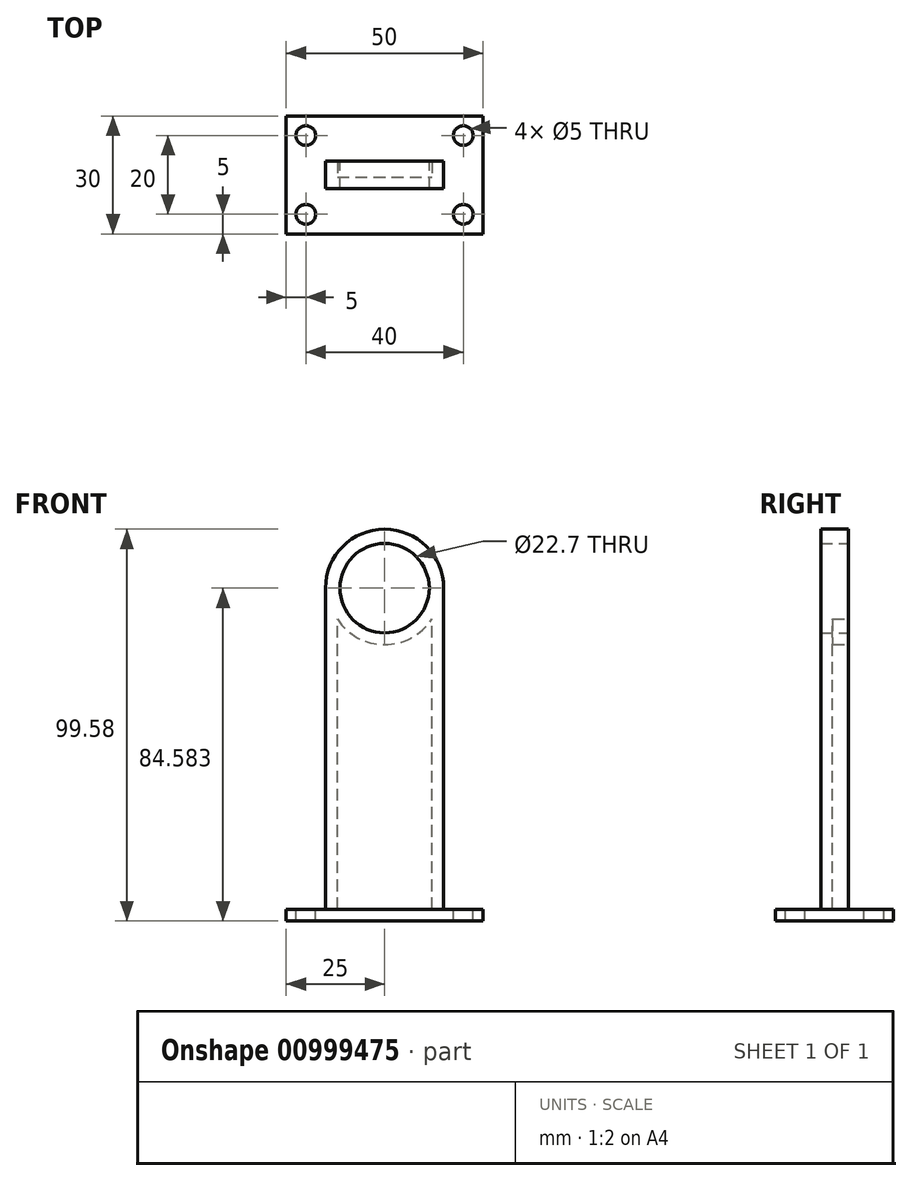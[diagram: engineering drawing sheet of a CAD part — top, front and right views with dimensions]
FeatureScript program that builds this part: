
annotation { "Feature Type Name" : "Feature", "Feature Type Description" : "" }
export const myFeature = defineFeature(function(context is Context, id is Id, definition is map)
    precondition{}
    {
        {
            var Q0;
            Q0=qCreatedBy(makeId("Front.planeOp"),FACE);
            var sketch = newSketch(context, id + "F0", { "sketchPlane" : qUnion([Q0])});
            skLineSegment(sketch, "E0.top", {"start": v(-25, -50) * mm, "end": v(25, -50) * mm});
            skLineSegment(sketch, "E0.right", {"start": v(25, -47) * mm, "end": v(25, -50) * mm});
            skPoint(sketch, "E0.middle", {"position": v(0, 0) * mm});
            skLineSegment(sketch, "E1", {"start": v(0, 50) * mm, "end": v(0, 49.58) * mm, "construction": true});
            skLineSegment(sketch, "E2", {"start": v(-15, 0) * mm, "end": v(15, 0) * mm});
            skCircle(sketch, "E3", {"center": v(0, 34.58) * mm, "radius": 11.35 * mm});
            skLineSegment(sketch, "E4", {"start": v(25, -47) * mm, "end": v(-25, -47) * mm});
            skLineSegment(sketch, "E5", {"start": v(15, -47) * mm, "end": v(15, 34.58) * mm});
            skLineSegment(sketch, "E6", {"start": v(-15, -47) * mm, "end": v(-15, 34.58) * mm});
            skCircle(sketch, "E7", {"center": v(0, 34.58) * mm, "radius": 15 * mm});
            skLineSegment(sketch, "E8.trimOffspring", {"start": v(0, 19.58) * mm, "end": v(0, -47) * mm});
            skPoint(sketch, "E9.orphan", {"position": v(-25, 0) * mm});
            skPoint(sketch, "E10.orphan", {"position": v(25, 0) * mm});
            skPoint(sketch, "E11.orphan", {"position": v(0, -50) * mm});
            skLineSegment(sketch, "E12.trimOffspring", {"start": v(-25, -47) * mm, "end": v(-25, -50) * mm});
            skPoint(sketch, "E13.orphan", {"position": v(25, 50) * mm});
            skPoint(sketch, "E0.bottom.start.orphan", {"position": v(-25, 50) * mm});
            skSolve(sketch);
        }
        {
            var Q0;
            {var subQ0=sQuery(id+"F0.wireOp",EDGE,"E5");Q0=makeQuery(id+"F0.imprint","IMPRINT",FACE,{"disambiguationData":[TD([[makeQuery(id+"F0.imprint","IMPRINT",EDGE,{"derivedFrom":subQ0}),1.0]])]});}
            var Q1;
            Q1=makeQuery(id+"F0.imprint","IMPRINT",FACE,{"disambiguationData":[TD([[makeQuery(id+"F0.imprint","IMPRINT",EDGE,{"derivedFrom":sQuery(id+"F0.wireOp",EDGE,"E3")}),-1.0]])]});
            var Q2;
            {var subQ0=sQuery(id+"F0.wireOp",EDGE,"E6");var subQ1=sQuery(id+"F0.wireOp",EDGE,"E2");var subQ2=makeQuery(id+"F0.imprint","INTERSECT",VERTEX,{"derivedFrom":[subQ1,subQ0]});Q2=makeQuery(id+"F0.imprint","IMPRINT",FACE,{"disambiguationData":[TD([[makeQuery(id+"F0.imprint","IMPRINT",EDGE,{"disambiguationData":[TD([[subQ2,-1.0]])],"derivedFrom":subQ1}),1.0]])]});}
            var Q3;
            {var subQ0=sQuery(id+"F0.wireOp",EDGE,"E6");var subQ1=sQuery(id+"F0.wireOp",EDGE,"E2");var subQ2=makeQuery(id+"F0.imprint","INTERSECT",VERTEX,{"derivedFrom":[subQ1,subQ0]});Q3=makeQuery(id+"F0.imprint","IMPRINT",FACE,{"disambiguationData":[TD([[makeQuery(id+"F0.imprint","IMPRINT",EDGE,{"disambiguationData":[TD([[subQ2,-1.0]])],"derivedFrom":subQ1}),-1.0]])]});}
            extrude(context, id + "F1", {"entities" : qUnion([Q0, Q1, Q2, Q3]), "depth" : 7 * mm, "offsetDistance" : 25 * mm, "symmetric" : true});
        }
        {
            var Q0;
            Q0=makeQuery(id+"F0.imprint","IMPRINT",FACE,{"disambiguationData":[TD([[makeQuery(id+"F0.imprint","IMPRINT",EDGE,{"derivedFrom":sQuery(id+"F0.wireOp",EDGE,"E0.top")}),1.0]])]});
            extrude(context, id + "F2", {"entities" : qUnion([Q0]), "operationType" : NewBodyOperationType.ADD, "depth" : 30 * mm, "offsetDistance" : 25 * mm, "symmetric" : true});
        }
        {
            var Q0;
            Q0=makeQuery(id+"F1.opExtrude","CAP_FACE",FACE,{"disambiguationData":[OSD([sQuery(id+"F0.wireOp",EDGE,"E3"),sQuery(id+"F0.wireOp",EDGE,"E4"),sQuery(id+"F0.wireOp",EDGE,"E5"),sQuery(id+"F0.wireOp",EDGE,"E6"),sQuery(id+"F0.wireOp",EDGE,"E7")])],"isStart":true});
            shell(context, id + "F3", {"entities" : qUnion([Q0]), "thickness" : 3 * mm});
        }
        {
            var Q0;
            Q0=qCreatedBy(makeId("Top.planeOp"),FACE);
            var sketch = newSketch(context, id + "F4", { "sketchPlane" : qUnion([Q0])});
            skCircle(sketch, "E14", {"center": v(20, 10) * mm, "radius": 2.5 * mm});
            skCircle(sketch, "E15", {"center": v(20, -10) * mm, "radius": 2.5 * mm});
            skCircle(sketch, "E16", {"center": v(-20, -10) * mm, "radius": 2.5 * mm});
            skCircle(sketch, "E17", {"center": v(-20, 10) * mm, "radius": 2.5 * mm});
            skSolve(sketch);
        }
        {
            var Q0;
            Q0=makeQuery(id+"F4.imprint","IMPRINT",FACE,{"disambiguationData":[TD([[makeQuery(id+"F4.imprint","IMPRINT",EDGE,{"derivedFrom":sQuery(id+"F4.wireOp",EDGE,"E14")}),1.0]])]});
            var Q1;
            Q1=makeQuery(id+"F4.imprint","IMPRINT",FACE,{"disambiguationData":[TD([[makeQuery(id+"F4.imprint","IMPRINT",EDGE,{"derivedFrom":sQuery(id+"F4.wireOp",EDGE,"E17")}),1.0]])]});
            var Q2;
            Q2=makeQuery(id+"F4.imprint","IMPRINT",FACE,{"disambiguationData":[TD([[makeQuery(id+"F4.imprint","IMPRINT",EDGE,{"derivedFrom":sQuery(id+"F4.wireOp",EDGE,"E16")}),1.0]])]});
            var Q3;
            Q3=makeQuery(id+"F4.imprint","IMPRINT",FACE,{"disambiguationData":[TD([[makeQuery(id+"F4.imprint","IMPRINT",EDGE,{"derivedFrom":sQuery(id+"F4.wireOp",EDGE,"E15")}),1.0]])]});
            var Q4;
            Q4=makeQuery(id+"F2.opExtrude","SWEPT_FACE",FACE,{"disambiguationData":[OSD([sQuery(id+"F0.wireOp",EDGE,"E0.top")])]});
            extrude(context, id + "F5", {"entities" : qUnion([Q0, Q1, Q2, Q3]), "operationType" : NewBodyOperationType.REMOVE, "oppositeDirection" : true, "depth" : 56 * mm, "endBoundEntityFace" : qUnion([Q4]), "offsetDistance" : 25 * mm});
        }
    });
